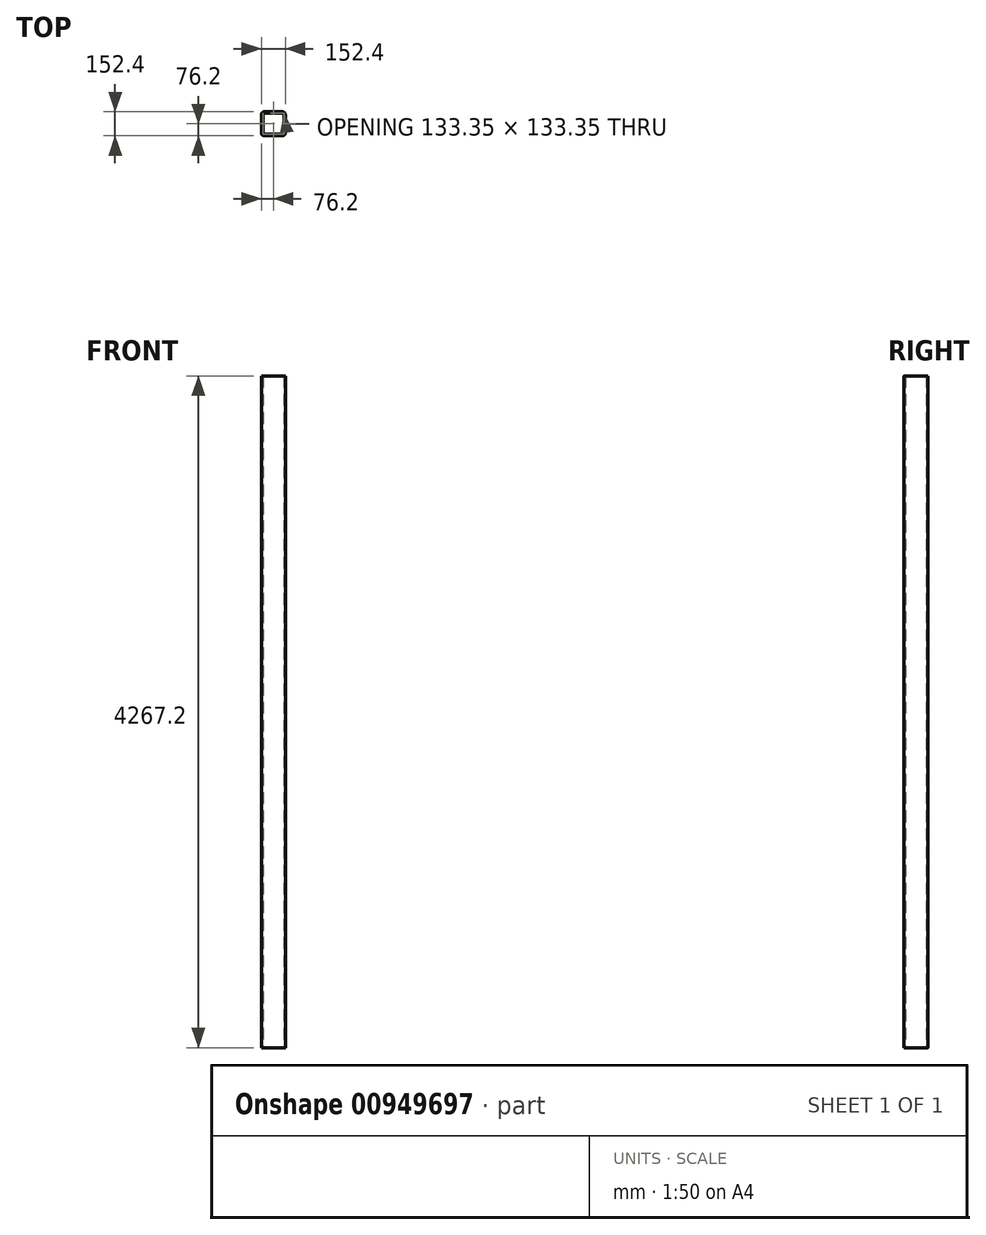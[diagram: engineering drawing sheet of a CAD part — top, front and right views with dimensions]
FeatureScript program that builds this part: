
annotation { "Feature Type Name" : "Feature", "Feature Type Description" : "" }
export const myFeature = defineFeature(function(context is Context, id is Id, definition is map)
    precondition{}
    {
        {
            var Q0;
            Q0=qCreatedBy(makeId("Top.planeOp"),FACE);
            var sketch = newSketch(context, id + "F0", { "sketchPlane" : qUnion([Q0])});
            skLineSegment(sketch, "E0.bottom", {"start": v(-57.15, -76.2) * mm, "end": v(57.15, -76.2) * mm});
            skLineSegment(sketch, "E0.top", {"start": v(-57.15, 76.2) * mm, "end": v(57.15, 76.2) * mm});
            skLineSegment(sketch, "E0.left", {"start": v(-76.2, -57.15) * mm, "end": v(-76.2, 57.15) * mm});
            skLineSegment(sketch, "E0.right", {"start": v(76.2, -57.15) * mm, "end": v(76.2, 57.15) * mm});
            skPoint(sketch, "E0.middle", {"position": v(0, 0) * mm});
            skLineSegment(sketch, "E1.bottom", {"start": v(-57.15, -66.68) * mm, "end": v(57.15, -66.68) * mm});
            skLineSegment(sketch, "E1.top", {"start": v(-57.15, 66.68) * mm, "end": v(57.15, 66.68) * mm});
            skLineSegment(sketch, "E1.left", {"start": v(-66.68, -57.15) * mm, "end": v(-66.68, 57.15) * mm});
            skLineSegment(sketch, "E1.right", {"start": v(66.68, -57.15) * mm, "end": v(66.68, 57.15) * mm});
            skPoint(sketch, "E2.visualSharp", {"position": v(-76.2, 76.2) * mm});
            skArc(sketch, "E2.filletArc", {"start": v(-57.15, 76.2) * mm, "mid": v(-70.62, 70.62) * mm, "end": v(-76.2, 57.15) * mm});
            skPoint(sketch, "E3.visualSharp", {"position": v(-76.2, -76.2) * mm});
            skArc(sketch, "E3.filletArc", {"start": v(-76.2, -57.15) * mm, "mid": v(-70.62, -70.62) * mm, "end": v(-57.15, -76.2) * mm});
            skPoint(sketch, "E4.visualSharp", {"position": v(76.2, -76.2) * mm});
            skArc(sketch, "E4.filletArc", {"start": v(57.15, -76.2) * mm, "mid": v(70.62, -70.62) * mm, "end": v(76.2, -57.15) * mm});
            skPoint(sketch, "E5.visualSharp", {"position": v(76.2, 76.2) * mm});
            skArc(sketch, "E5.filletArc", {"start": v(76.2, 57.15) * mm, "mid": v(70.62, 70.62) * mm, "end": v(57.15, 76.2) * mm});
            skPoint(sketch, "E6.visualSharp", {"position": v(-66.68, 66.68) * mm});
            skArc(sketch, "E6.filletArc", {"start": v(-57.15, 66.68) * mm, "mid": v(-63.89, 63.89) * mm, "end": v(-66.68, 57.15) * mm});
            skPoint(sketch, "E7.visualSharp", {"position": v(-66.68, -66.68) * mm});
            skArc(sketch, "E7.filletArc", {"start": v(-66.68, -57.15) * mm, "mid": v(-63.89, -63.89) * mm, "end": v(-57.15, -66.68) * mm});
            skPoint(sketch, "E8.visualSharp", {"position": v(66.68, -66.68) * mm});
            skArc(sketch, "E8.filletArc", {"start": v(57.15, -66.68) * mm, "mid": v(63.89, -63.89) * mm, "end": v(66.68, -57.15) * mm});
            skPoint(sketch, "E9.visualSharp", {"position": v(66.68, 66.68) * mm});
            skArc(sketch, "E9.filletArc", {"start": v(66.68, 57.15) * mm, "mid": v(63.89, 63.89) * mm, "end": v(57.15, 66.68) * mm});
            skSolve(sketch);
        }
        {
            var Q0;
            Q0=qSketchRegion(id+"F0",true);
            extrude(context, id + "F1", {"entities" : qUnion([Q0]), "depth" : 4267.2 * mm, "offsetDistance" : 25.4 * mm});
        }
    });
